# Revit family: rechteck_wandausleger_671231_002_89_f2ff
name_source: partatom
category: Lighting Fixtures
units: mm (PartAtom-declared; Revit-internal decimal feet)

## family parameters
Cut with Voids When Loaded = No
Host = Face
Light Source = No
Part Type = Normal
Room Calculation Point = No
Round Connector Dimension = Use Diameter
Shared = No

## types (1)
- RECHTECK wandausleger
    Apparent Load = 0 VA
    Default Elevation = 1800 mm
    Description = Series: RECHTECK
Rectangular wall extension luminaire in classic design. For escape route identification. Housing: aluminium, with plastic corner connectors. Display panels: plastic, opal, with motifs on one side/on both sides. Wall extension Driver integrated. Suitable for connection to central battery systems. With AC Control monitoring module for LUXIFAIR central battery units. Please indicate legend number when placing your order! 
Colour: white
Length: 485 mm
Width: 125 mm
Height: 250 mm
Weight: 2.78 kg
Operating mode: maintained power mode
Viewing Distance: 43 m
Lamp: LED
Socket: without socket
Colour temperature: 6500K
Colour rendering index (CRI): 70
System power: 9.1 W
Control gear: Regulated power supply
Protection class: I
Type of protection: IP 44
    Height = 250 mm
    Lamp = 0 x
    Length = 485 mm
    Luminous efficacy = 0 lm/W
    Manufacturer = RZB
    ModVariant = No
    Model = 671231.002.89
    Mounting Place = Wall
    Mounting Type = Surface mounted
    Number of Poles = 1
    OnlyDefault = Yes
    Power Factor = 1
    Product Name = RECHTECK wandausleger
    Product group = wall cantilever luminaires
    ProductGroupID = 2005
    Protection Class = Protection class I
    Protection Degree = IP 44
    RLX_Detail_Level = 1
    RLX_Emergency_Light_Flux = 0 lm
    RLX_Emergency_Type = 0
    RLX_Emergency_Type_DB = No
    RlxData = <blob elided: 41149 chars, md5=2b8a0048>
    Standby Power = 0 W
    System Light Flux = 0 lm
    System Power = 0 W
    Type Comments = Product without accessories
    Type Image = 671081.002.jpg
    URL = http://relux.com
    VarID = ---
    Voltage = 230 V
    Voltage Range = 220-240 V
    Weight = 0.00 kg
    Width = 125 mm

## geometry (parser evidence)
native form markers: Sweep x12
no freeform markers — native parametric forms only
